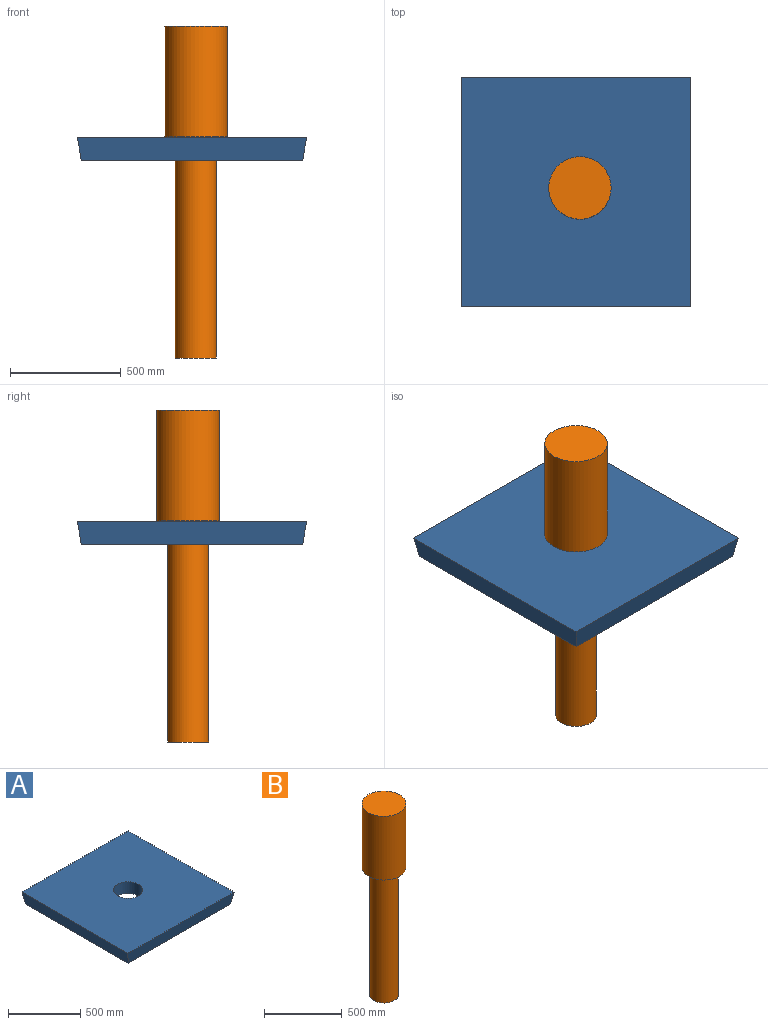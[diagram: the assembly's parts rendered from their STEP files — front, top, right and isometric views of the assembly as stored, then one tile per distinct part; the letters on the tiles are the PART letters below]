
ASSEMBLY  parts=2 mates=1
PART A: 7 faces, bbox 1035.3x1035.3x100 mm
  f0: plane 1035.27x100mm, normal (0,0.98,-0.17), area 103333.1mm2, adj f1,f3,f4,f5
  f1: plane 1035.27x100mm, normal (-0.98,0,-0.17), area 103333.1mm2, adj f0,f2,f4,f5
  f2: plane 1035.27x100mm, normal (0,-0.98,-0.17), area 103333.1mm2, adj f1,f3,f4,f5
  f3: plane 1035.27x100mm, normal (0.98,0,-0.17), area 103333.1mm2, adj f0,f2,f4,f5
  f4: plane 1035.27x1035.27mm, normal (0,0,1), area 1040358.5mm2, adj f0,f1,f2,f3,f6
  f5: plane 1000x1000mm, normal (0,0,-1), area 968584.1mm2, adj f0,f1,f2,f3,f6
  f6: cylinder r=100mm len=200mm, axis (0,0,1), area 62831.9mm2, adj f4,f5
PART B: 5 faces, bbox 282.3x282.3x1500 mm
  f0: cylinder r=92.48mm len=1000mm, axis (0,0,1), area 581063.2mm2, adj f1,f4
  f1: plane 184.96x184.96mm, normal (0,0,-1), area 26868.1mm2, adj f0
  f2: cylinder r=141.15mm len=500mm, axis (0,0,-1), area 443429.7mm2, adj f3,f4
  f3: plane 282.3x282.3mm, normal (0,0,1), area 62589.2mm2, adj f2
  f4: plane 282.3x282.3mm, normal (0,0,-1), area 35721.1mm2, adj f0,f2
PLACE A rot(axis=(0.84,0.55,0),0deg) t=(-77.55,-731.84,-992.16)mm
PLACE B t=(-77.55,-731.84,-986.42)mm
MATE slider A.f6 <-> B.f0  axis (0,0,1) through (440.08,-1214.2,-942.16)mm
